# Revit family: door
name_source: partatom
category: Doors
revit_build: Autodesk Revit 2016 (Build: 20150714_1515(x64)
units: mm (PartAtom-declared; Revit-internal decimal feet)

## family parameters
Always vertical = Yes
Cut with Voids When Loaded = No
Host = Wall
OmniClass Number = 23.30.10.00
OmniClass Title = Doors
Room Calculation Point = No
Shared = No

## types (7) — shared parameters
Analytic Construction = Metal
Assembly Code = C1020
Construction Type Id = MDOOR
Door Material = Door - Panel
Frame Material = Door - Frame
Function = Interior
Heat Transfer Coefficient (U) = 0.6520 BTU/(h·ft²·°F)
Height = 6' - 8"
HeightFeet = 6
HeightInches = 8
HeightReal = 6.666667
Thermal Resistance (R) = 1.5338 (h·ft²·°F)/BTU
Thickness = 0' - 2"
Trim Projection Ext = 0' - 1"
Trim Projection Int = 0' - 1"
Trim Width = 0' - 3"
Wall Closure = By host
zero-valued in all types: Solar Heat Gain Coefficient, Visual Light Transmittance

## per-type parameters (varying)
| type | Width | WidthFeet | WidthInches | WidthReal |
| 2' 4" x 6' 8" | 2' - 4" | 2 | 4 | 2.333333 |
| 2' 6" x 6' 8" | 2' - 6" | 2 | 6 | 2.5 |
| 2' 8" x 6' 8" | 2' - 8" | 2 | 8 | 2.666667 |
| 2' 10" x 6' 8" | 2' - 10" | 2 | 10 | 2.833333 |
| 3' 0" x 6' 8" | 3' - 0" | 3 | 0 | 3 |
| 1'-6" x 6' 8" | 1' - 6" | 1 | 6 | 1.5 |
| 2' 0" x 6' 8" | 2' - 0" | 2 | 0 | 2 |

## geometry (parser evidence)
native form markers: Blend x6, Sweep x3
no freeform markers — native parametric forms only
